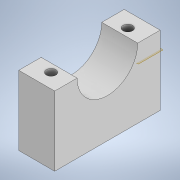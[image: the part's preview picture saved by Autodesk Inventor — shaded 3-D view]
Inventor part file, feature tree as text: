
AUTODESK INVENTOR PART (.ipt)
format: ipt  version: 2020 (Build 240168000, 168)  size: 121,856 bytes
history: native  units: mm
features: extrude x3, sketch x3, other x2
ambient origin geometry x8: Origin, YZ Plane, XZ Plane, XY Plane, X Axis, Y Axis, Z Axis, Center Point
bodies: Body1 (feature_tree)
feature tree (8):
  other  "Твердое тело1"
  extrude  "Выдавливание1"  Depth=15.0mm
  extrude  "Выдавливание2"  Depth=44.0mm
  other  "РабПлоскость1"
  extrude  "Выдавливание3"  Depth=16.0mm
  sketch  "Эскиз1"
  sketch  "Эскиз2"
  sketch  "Эскиз3"
